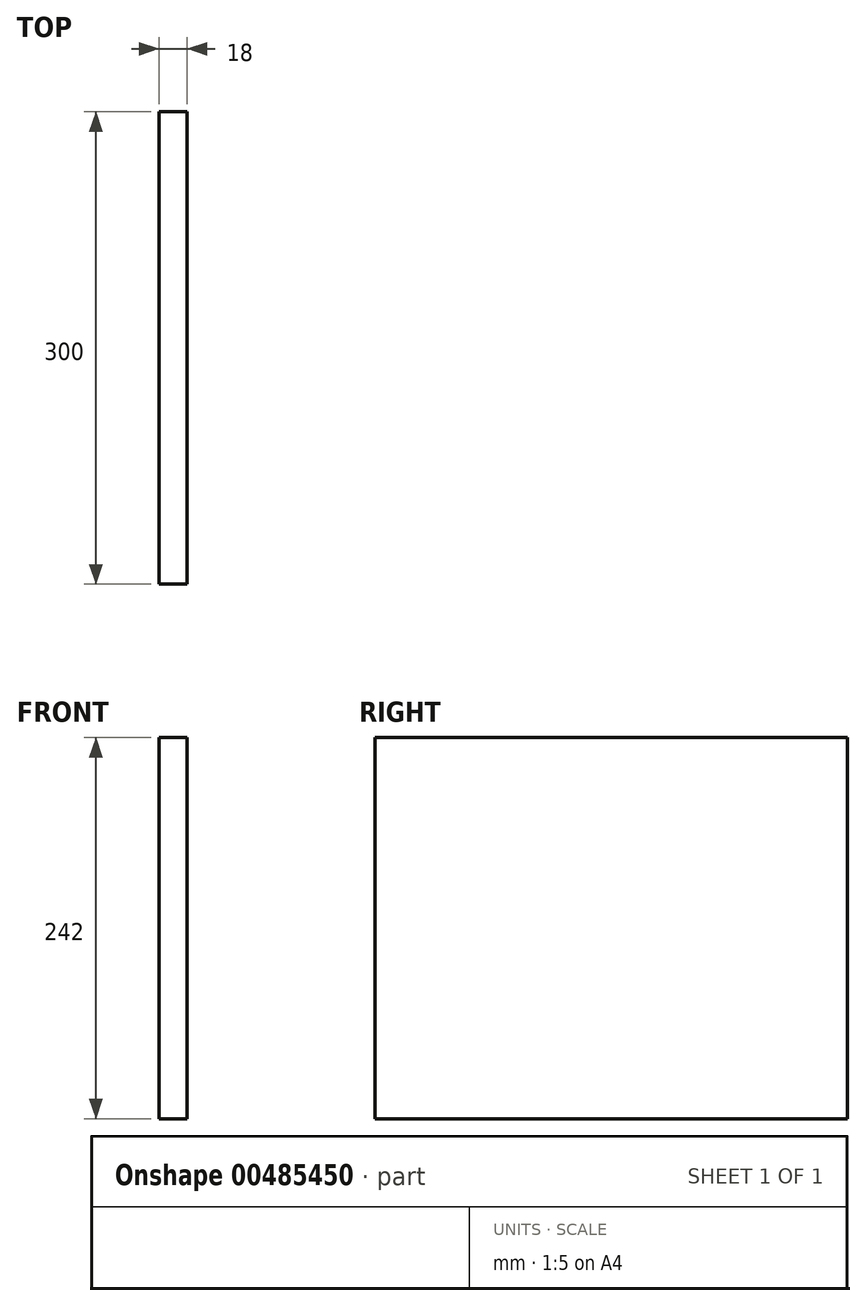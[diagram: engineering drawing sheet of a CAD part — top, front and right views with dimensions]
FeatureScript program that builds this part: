
annotation { "Feature Type Name" : "Feature", "Feature Type Description" : "" }
export const myFeature = defineFeature(function(context is Context, id is Id, definition is map)
    precondition{}
    {
        {
            var Q0;
            Q0=qCreatedBy(makeId("Top.planeOp"),FACE);
            var sketch = newSketch(context, id + "F0", { "sketchPlane" : qUnion([Q0])});
            skLineSegment(sketch, "E0.bottom", {"start": v(9, 150) * mm, "end": v(-9, 150) * mm});
            skLineSegment(sketch, "E0.top", {"start": v(9, -150) * mm, "end": v(-9, -150) * mm});
            skLineSegment(sketch, "E0.left", {"start": v(9, 150) * mm, "end": v(9, -150) * mm});
            skLineSegment(sketch, "E0.right", {"start": v(-9, 150) * mm, "end": v(-9, -150) * mm});
            skPoint(sketch, "E0.middle", {"position": v(0, 0) * mm});
            skSolve(sketch);
        }
        {
            var Q0;
            Q0 = qSketchRegion(id + "F0", true);
            extrude(context, id + "F1", {"entities" : qUnion([Q0]), "depth" : 242 * mm});
        }
    });
